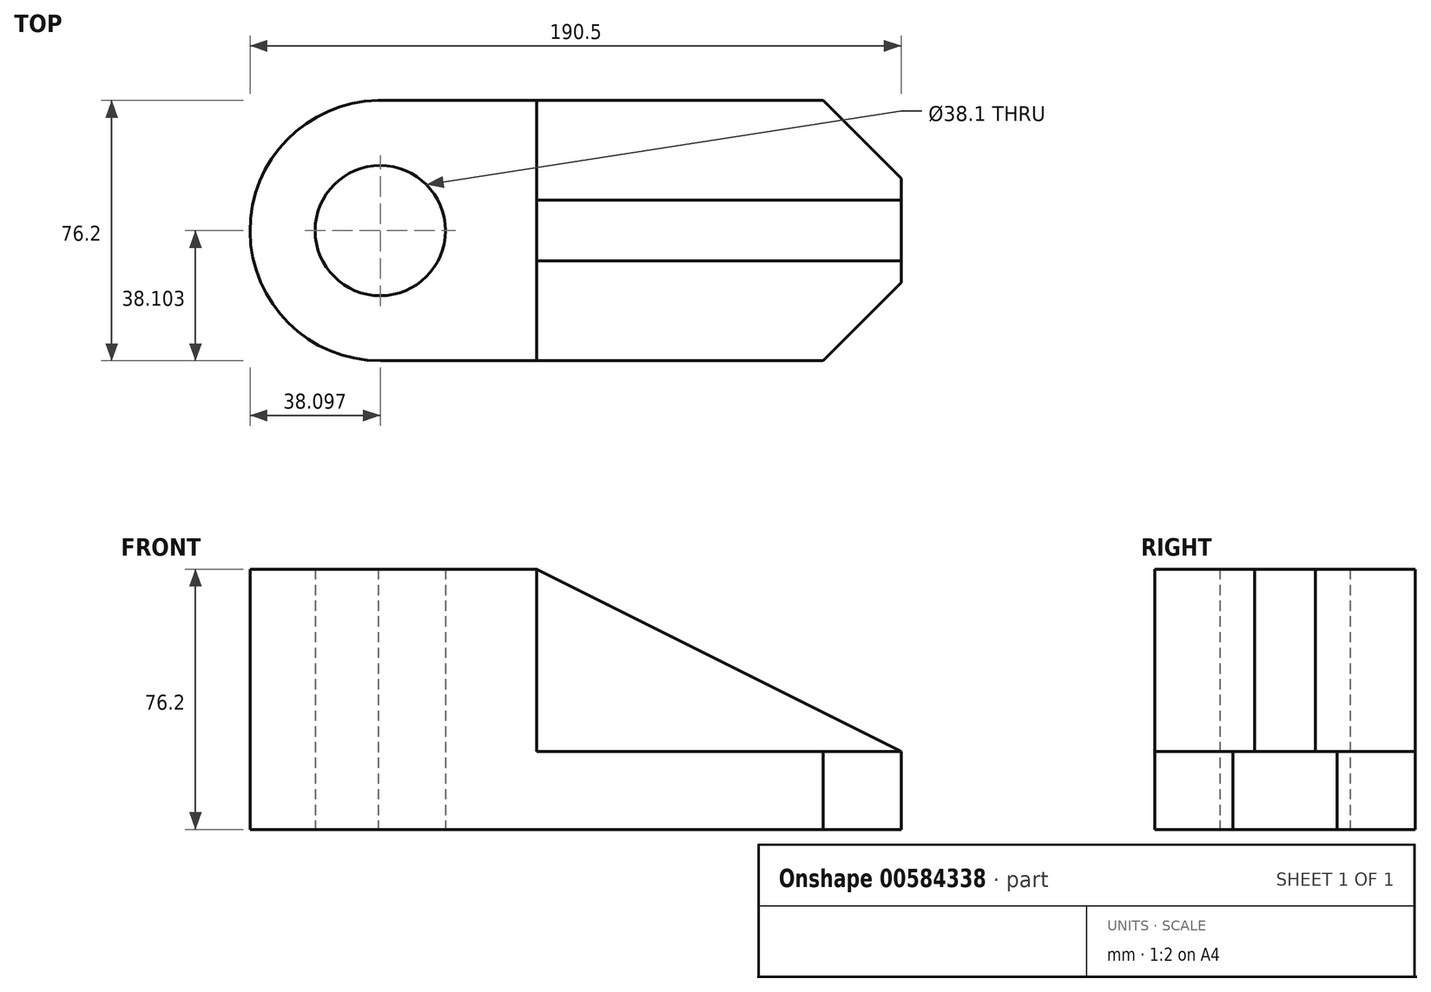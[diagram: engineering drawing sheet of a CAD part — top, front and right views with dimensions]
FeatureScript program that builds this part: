
annotation { "Feature Type Name" : "Feature", "Feature Type Description" : "" }
export const myFeature = defineFeature(function(context is Context, id is Id, definition is map)
    precondition{}
    {
        {
            var Q0;
            Q0=qCreatedBy(makeId("Top.planeOp"),FACE);
            var sketch = newSketch(context, id + "F0", { "sketchPlane" : qUnion([Q0])});
            skCircle(sketch, "E0", {"center": v(-27.3, 33.14) * mm, "radius": 19.05 * mm});
            skArc(sketch, "E1", {"start": v(-26.66, 71.24) * mm, "mid": v(-65.4, 33.46) * mm, "end": v(-27.3, -4.96) * mm});
            skLineSegment(sketch, "E2", {"start": v(125.1, 48.38) * mm, "end": v(125.1, 17.9) * mm});
            skLineSegment(sketch, "E3", {"start": v(-27.3, -4.96) * mm, "end": v(102.24, -4.96) * mm});
            skLineSegment(sketch, "E4", {"start": v(-27.94, 71.24) * mm, "end": v(102.24, 71.24) * mm});
            skLineSegment(sketch, "E5", {"start": v(102.24, -4.96) * mm, "end": v(125.1, 17.9) * mm});
            skLineSegment(sketch, "E6", {"start": v(102.24, 71.24) * mm, "end": v(125.1, 48.38) * mm});
            skLineSegment(sketch, "E7", {"start": v(18.42, 71.24) * mm, "end": v(18.42, -4.96) * mm});
            skLineSegment(sketch, "E8", {"start": v(125.1, 42.03) * mm, "end": v(18.42, 42.03) * mm});
            skPoint(sketch, "E8.endSnap0", {"position": v(18.42, 33.14) * mm});
            skLineSegment(sketch, "E9", {"start": v(125.1, 24.25) * mm, "end": v(18.42, 24.25) * mm});
            skSolve(sketch);
        }
        {
            var Q0;
            Q0=makeQuery(id+"F0.imprint","IMPRINT",FACE,{"disambiguationData":[TD([[makeQuery(id+"F0.imprint","IMPRINT",EDGE,{"derivedFrom":sQuery(id+"F0.wireOp",EDGE,"E0")}),-1.0]])]});
            extrude(context, id + "F1", {"entities" : qUnion([Q0]), "depth" : 76.2 * mm, "offsetDistance" : 25.4 * mm});
        }
        {
            var Q0;
            {var subQ0=sQuery(id+"F0.wireOp",EDGE,"E6");Q0=makeQuery(id+"F0.imprint","IMPRINT",FACE,{"disambiguationData":[TD([[makeQuery(id+"F0.imprint","IMPRINT",EDGE,{"derivedFrom":subQ0}),-1.0]])]});}
            var Q1;
            {var subQ0=sQuery(id+"F0.wireOp",EDGE,"E5");Q1=makeQuery(id+"F0.imprint","IMPRINT",FACE,{"disambiguationData":[TD([[makeQuery(id+"F0.imprint","IMPRINT",EDGE,{"derivedFrom":subQ0}),1.0]])]});}
            extrude(context, id + "F2", {"entities" : qUnion([Q0, Q1]), "operationType" : NewBodyOperationType.ADD, "depth" : 22.86 * mm, "offsetDistance" : 25.4 * mm});
        }
        {
            var Q0;
            {var subQ0=sQuery(id+"F0.wireOp",EDGE,"E8");Q0=makeQuery(id+"F0.imprint","IMPRINT",FACE,{"disambiguationData":[TD([[makeQuery(id+"F0.imprint","IMPRINT",EDGE,{"derivedFrom":subQ0}),1.0]])]});}
            extrude(context, id + "F3", {"entities" : qUnion([Q0]), "operationType" : NewBodyOperationType.ADD, "depth" : 76.2 * mm, "offsetDistance" : 25.4 * mm});
        }
        {
            var Q0;
            Q0=makeQuery(id+"F3.opExtrude","SWEPT_FACE",FACE,{"disambiguationData":[OSD([sQuery(id+"F0.wireOp",EDGE,"E9")])]});
            var sketch = newSketch(context, id + "F4", { "sketchPlane" : qUnion([Q0])});
            skLineSegment(sketch, "E10", {"start": v(18.42, 76.2) * mm, "end": v(125.1, 22.86) * mm});
            skSolve(sketch);
        }
        {
            var Q0;
            Q0=makeQuery(id+"F4.imprint","IMPRINT",FACE,{"disambiguationData":[TD([[makeQuery(id+"F4.imprint","IMPRINT",EDGE,{"derivedFrom":sQuery(id+"F4.wireOp",EDGE,"E10")}),1.0]])]});
            extrude(context, id + "F5", {"entities" : qUnion([Q0]), "operationType" : NewBodyOperationType.REMOVE, "oppositeDirection" : true, "depth" : 25.4 * mm, "offsetDistance" : 25.4 * mm});
        }
    });
